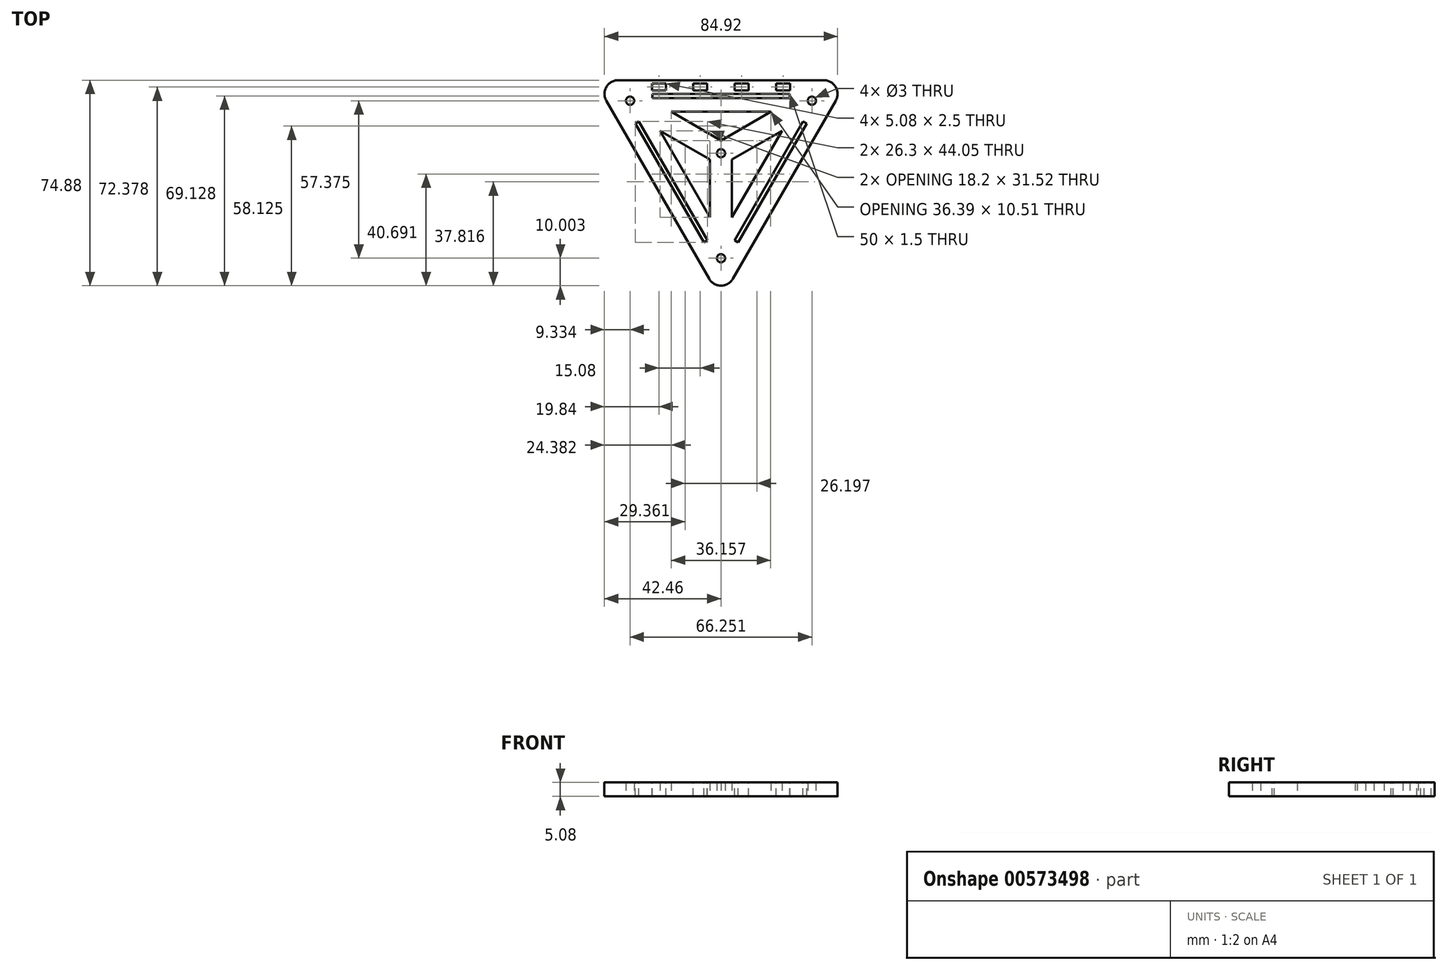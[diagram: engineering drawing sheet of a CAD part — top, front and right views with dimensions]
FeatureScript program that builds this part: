
annotation { "Feature Type Name" : "Feature", "Feature Type Description" : "" }
export const myFeature = defineFeature(function(context is Context, id is Id, definition is map)
    precondition{}
    {
        {
            var Q0;
            Q0=qCreatedBy(makeId("Top.planeOp"),FACE);
            var sketch = newSketch(context, id + "F0", { "sketchPlane" : qUnion([Q0])});
            skLineSegment(sketch, "E0", {"start": v(-33.13, 70.62) * mm, "end": v(33.13, 70.62) * mm, "construction": true});
            skLineSegment(sketch, "E1", {"start": v(33.13, 70.62) * mm, "end": v(0, 13.24) * mm, "construction": true});
            skLineSegment(sketch, "E2", {"start": v(0, 13.24) * mm, "end": v(-33.13, 70.62) * mm, "construction": true});
            skCircle(sketch, "E3", {"center": v(-33.13, 70.62) * mm, "radius": 1.5 * mm});
            skCircle(sketch, "E4", {"center": v(33.13, 70.62) * mm, "radius": 1.5 * mm});
            skCircle(sketch, "E5", {"center": v(0, 13.24) * mm, "radius": 1.5 * mm});
            skCircle(sketch, "E6", {"center": v(0, 51.5) * mm, "radius": 1.5 * mm});
            skPoint(sketch, "E6.centerSnap0", {"position": v(0, 70.62) * mm});
            skLineSegment(sketch, "E7", {"start": v(0, 51.5) * mm, "end": v(-33.13, 70.62) * mm, "construction": true});
            skLineSegment(sketch, "E8", {"start": v(0, 51.5) * mm, "end": v(33.13, 70.62) * mm, "construction": true});
            skLineSegment(sketch, "E9", {"start": v(0, 51.5) * mm, "end": v(0, 13.24) * mm, "construction": true});
            skLineSegment(sketch, "E10", {"start": v(0, -1.76) * mm, "end": v(46.12, 78.12) * mm});
            skLineSegment(sketch, "E11", {"start": v(33.13, 70.62) * mm, "end": v(46.12, 78.12) * mm});
            skLineSegment(sketch, "E12", {"start": v(46.12, 78.12) * mm, "end": v(0, 78.12) * mm});
            skLineSegment(sketch, "E13.MirrorCS", {"start": v(-46.12, 78.12) * mm, "end": v(0, 78.12) * mm});
            skLineSegment(sketch, "E14.MirrorCS", {"start": v(-33.13, 70.62) * mm, "end": v(-46.12, 78.12) * mm});
            skLineSegment(sketch, "E15.MirrorCS", {"start": v(0, -1.76) * mm, "end": v(-46.12, 78.12) * mm});
            skLineSegment(sketch, "E16", {"start": v(0, 66.62) * mm, "end": v(26.2, 66.62) * mm});
            skLineSegment(sketch, "E17", {"start": v(26.2, 66.62) * mm, "end": v(0, 21.24) * mm});
            skLineSegment(sketch, "E18.MirrorCS", {"start": v(0, 66.62) * mm, "end": v(-26.2, 66.62) * mm});
            skLineSegment(sketch, "E19.MirrorCS", {"start": v(-26.2, 66.62) * mm, "end": v(0, 21.24) * mm});
            skLineSegment(sketch, "E20", {"start": v(-22.2, 59.7) * mm, "end": v(-4, 49.18) * mm});
            skLineSegment(sketch, "E21", {"start": v(-4, 49.18) * mm, "end": v(-4, 28.17) * mm});
            skLineSegment(sketch, "E22", {"start": v(-18.2, 66.62) * mm, "end": v(0, 56.11) * mm});
            skLineSegment(sketch, "E23.MirrorCS", {"start": v(18.2, 66.62) * mm, "end": v(0, 56.11) * mm});
            skLineSegment(sketch, "E24.MirrorCS", {"start": v(22.2, 59.7) * mm, "end": v(4, 49.18) * mm});
            skLineSegment(sketch, "E25.MirrorCS", {"start": v(4, 49.18) * mm, "end": v(4, 28.17) * mm});
            skSolve(sketch);
        }
        {
            var Q0;
            Q0=makeQuery(id+"F0.imprint","IMPRINT",FACE,{"disambiguationData":[TD([[makeQuery(id+"F0.imprint","IMPRINT",EDGE,{"derivedFrom":sQuery(id+"F0.wireOp",EDGE,"E3")}),-1.0]])]});
            var Q1;
            Q1=makeQuery(id+"F0.imprint","IMPRINT",FACE,{"disambiguationData":[TD([[makeQuery(id+"F0.imprint","IMPRINT",EDGE,{"derivedFrom":sQuery(id+"F0.wireOp",EDGE,"E6")}),-1.0]])]});
            extrude(context, id + "F1", {"entities" : qUnion([Q0, Q1]), "depth" : 5.08 * mm, "offsetDistance" : 25 * mm});
        }
        {
            var Q0;
            Q0=makeQuery(id+"F1.opExtrude","SWEPT_EDGE",EDGE,{"disambiguationData":[OSD([sQuery(id+"F0.wireOp",EDGE,"E13.MirrorCS"),sQuery(id+"F0.wireOp",EDGE,"E15.MirrorCS")])]});
            var Q1;
            Q1=makeQuery(id+"F1.opExtrude","SWEPT_EDGE",EDGE,{"disambiguationData":[OSD([sQuery(id+"F0.wireOp",EDGE,"E10"),sQuery(id+"F0.wireOp",EDGE,"E15.MirrorCS")])]});
            var Q2;
            Q2=makeQuery(id+"F1.opExtrude","SWEPT_EDGE",EDGE,{"disambiguationData":[OSD([sQuery(id+"F0.wireOp",EDGE,"E10"),sQuery(id+"F0.wireOp",EDGE,"E12")])]});
            fillet(context, id + "F2", {"entities" : qUnion([Q0, Q1, Q2]), "radius" : 5 * mm, "tangentPropagation" : true, "allowEdgeOverflow" : false});
        }
        {
            var Q0;
            Q0=makeQuery(id+"F1.opExtrude","CAP_FACE",FACE,{"disambiguationData":[OSD([sQuery(id+"F0.wireOp",EDGE,"E3"),sQuery(id+"F0.wireOp",EDGE,"E4"),sQuery(id+"F0.wireOp",EDGE,"E5"),sQuery(id+"F0.wireOp",EDGE,"E6"),sQuery(id+"F0.wireOp",EDGE,"E10"),sQuery(id+"F0.wireOp",EDGE,"E12"),sQuery(id+"F0.wireOp",EDGE,"E13.MirrorCS"),sQuery(id+"F0.wireOp",EDGE,"E15.MirrorCS"),sQuery(id+"F0.wireOp",EDGE,"E16"),sQuery(id+"F0.wireOp",EDGE,"E17"),sQuery(id+"F0.wireOp",EDGE,"E18.MirrorCS"),sQuery(id+"F0.wireOp",EDGE,"E19.MirrorCS"),sQuery(id+"F0.wireOp",EDGE,"E20"),sQuery(id+"F0.wireOp",EDGE,"E21"),sQuery(id+"F0.wireOp",EDGE,"E22"),sQuery(id+"F0.wireOp",EDGE,"E23.MirrorCS"),sQuery(id+"F0.wireOp",EDGE,"E24.MirrorCS"),sQuery(id+"F0.wireOp",EDGE,"E25.MirrorCS")])],"isStart":false});
            var sketch = newSketch(context, id + "F3", { "sketchPlane" : qUnion([Q0])});
            skLineSegment(sketch, "E26", {"start": v(0, 78.12) * mm, "end": v(0, 66.62) * mm, "construction": true});
            skLineSegment(sketch, "E27.bottom", {"start": v(25, 73.12) * mm, "end": v(-25, 73.12) * mm});
            skLineSegment(sketch, "E27.top", {"start": v(25, 71.62) * mm, "end": v(-25, 71.62) * mm});
            skLineSegment(sketch, "E27.left", {"start": v(25, 73.12) * mm, "end": v(25, 71.62) * mm});
            skLineSegment(sketch, "E27.right", {"start": v(-25, 73.12) * mm, "end": v(-25, 71.62) * mm});
            skPoint(sketch, "E27.middle", {"position": v(0, 72.37) * mm});
            skLineSegment(sketch, "E28", {"start": v(-13.1, 43.93) * mm, "end": v(-23.06, 38.18) * mm, "construction": true});
            skLineSegment(sketch, "E29", {"start": v(13.1, 43.93) * mm, "end": v(23.06, 38.18) * mm, "construction": true});
            skLineSegment(sketch, "E30", {"start": v(-18.08, 41.06) * mm, "end": v(-5.58, 19.4) * mm, "construction": true});
            skLineSegment(sketch, "E31", {"start": v(-5.58, 19.4) * mm, "end": v(-4.93, 19.78) * mm});
            skLineSegment(sketch, "E32", {"start": v(-4.93, 19.78) * mm, "end": v(-17.43, 41.43) * mm});
            skLineSegment(sketch, "E33.MirrorCS", {"start": v(-6.23, 19.03) * mm, "end": v(-18.73, 40.68) * mm});
            skLineSegment(sketch, "E34.MirrorCS", {"start": v(-5.58, 19.4) * mm, "end": v(-6.23, 19.03) * mm});
            skLineSegment(sketch, "E35.MirrorCS", {"start": v(-29.93, 63.08) * mm, "end": v(-17.43, 41.43) * mm});
            skLineSegment(sketch, "E36.MirrorCS", {"start": v(-31.23, 62.33) * mm, "end": v(-18.73, 40.68) * mm});
            skLineSegment(sketch, "E37.MirrorCS", {"start": v(-18.08, 41.06) * mm, "end": v(-30.58, 62.7) * mm, "construction": true});
            skLineSegment(sketch, "E38.MirrorCS", {"start": v(-30.58, 62.7) * mm, "end": v(-29.93, 63.08) * mm});
            skLineSegment(sketch, "E39.MirrorCS", {"start": v(-30.58, 62.7) * mm, "end": v(-31.23, 62.33) * mm});
            skLineSegment(sketch, "E40.MirrorCS", {"start": v(29.93, 63.08) * mm, "end": v(17.43, 41.43) * mm});
            skLineSegment(sketch, "E41.MirrorCS", {"start": v(31.23, 62.33) * mm, "end": v(18.73, 40.68) * mm});
            skLineSegment(sketch, "E42.MirrorCS", {"start": v(30.58, 62.7) * mm, "end": v(29.93, 63.08) * mm});
            skLineSegment(sketch, "E43.MirrorCS", {"start": v(30.58, 62.7) * mm, "end": v(31.23, 62.33) * mm});
            skLineSegment(sketch, "E44.MirrorCS", {"start": v(18.08, 41.06) * mm, "end": v(30.58, 62.7) * mm, "construction": true});
            skLineSegment(sketch, "E45.MirrorCS", {"start": v(5.58, 19.4) * mm, "end": v(4.93, 19.78) * mm});
            skLineSegment(sketch, "E46.MirrorCS", {"start": v(5.58, 19.4) * mm, "end": v(6.23, 19.03) * mm});
            skLineSegment(sketch, "E47.MirrorCS", {"start": v(18.08, 41.06) * mm, "end": v(5.58, 19.4) * mm, "construction": true});
            skLineSegment(sketch, "E48.MirrorCS", {"start": v(4.93, 19.78) * mm, "end": v(17.43, 41.43) * mm});
            skLineSegment(sketch, "E49.MirrorCS", {"start": v(6.23, 19.03) * mm, "end": v(18.73, 40.68) * mm});
            skLineSegment(sketch, "E50.bottom", {"start": v(5, 76.87) * mm, "end": v(10.08, 76.87) * mm});
            skLineSegment(sketch, "E50.top", {"start": v(5, 74.37) * mm, "end": v(10.08, 74.37) * mm});
            skLineSegment(sketch, "E50.left", {"start": v(5, 76.87) * mm, "end": v(5, 74.37) * mm});
            skLineSegment(sketch, "E50.right", {"start": v(10.08, 76.87) * mm, "end": v(10.08, 74.37) * mm});
            skPoint(sketch, "E50.middle", {"position": v(7.54, 75.62) * mm});
            skLineSegment(sketch, "E51", {"start": v(5, 75.62) * mm, "end": v(0, 75.62) * mm});
            skLineSegment(sketch, "E52.bottom", {"start": v(20.08, 76.87) * mm, "end": v(25.16, 76.87) * mm});
            skLineSegment(sketch, "E52.top", {"start": v(20.08, 74.37) * mm, "end": v(25.16, 74.37) * mm});
            skLineSegment(sketch, "E52.left", {"start": v(20.08, 76.87) * mm, "end": v(20.08, 74.37) * mm});
            skLineSegment(sketch, "E52.right", {"start": v(25.16, 76.87) * mm, "end": v(25.16, 74.37) * mm});
            skLineSegment(sketch, "E53.MirrorCS", {"start": v(-5, 76.87) * mm, "end": v(-10.08, 76.87) * mm});
            skLineSegment(sketch, "E54.MirrorCS", {"start": v(-5, 76.87) * mm, "end": v(-5, 74.37) * mm});
            skLineSegment(sketch, "E55.MirrorCS", {"start": v(-5, 74.37) * mm, "end": v(-10.08, 74.37) * mm});
            skLineSegment(sketch, "E56.MirrorCS", {"start": v(-10.08, 76.87) * mm, "end": v(-10.08, 74.37) * mm});
            skLineSegment(sketch, "E57.MirrorCS", {"start": v(-20.08, 76.87) * mm, "end": v(-25.16, 76.87) * mm});
            skLineSegment(sketch, "E58.MirrorCS", {"start": v(-25.16, 76.87) * mm, "end": v(-25.16, 74.37) * mm});
            skLineSegment(sketch, "E59.MirrorCS", {"start": v(-20.08, 74.37) * mm, "end": v(-25.16, 74.37) * mm});
            skLineSegment(sketch, "E60.MirrorCS", {"start": v(-20.08, 76.87) * mm, "end": v(-20.08, 74.37) * mm});
            skSolve(sketch);
        }
        {
            var Q0;
            {var subQ5=sQuery(id+"F3.wireOp",EDGE,"E27.right");Q0=makeQuery(id+"F3.imprint","IMPRINT",FACE,{"disambiguationData":[TD([[makeQuery(id+"F3.imprint","IMPRINT",EDGE,{"derivedFrom":subQ5}),1.0]])]});}
            var Q1;
            {var subQ5=sQuery(id+"F3.wireOp",EDGE,"E27.left");Q1=makeQuery(id+"F3.imprint","IMPRINT",FACE,{"disambiguationData":[TD([[makeQuery(id+"F3.imprint","IMPRINT",EDGE,{"derivedFrom":subQ5}),-1.0]])]});}
            var Q2;
            Q2=makeQuery(id+"F3.imprint","IMPRINT",FACE,{"disambiguationData":[TD([[makeQuery(id+"F3.imprint","IMPRINT",EDGE,{"derivedFrom":sQuery(id+"F3.wireOp",EDGE,"E31")}),1.0]])]});
            var Q3;
            Q3=makeQuery(id+"F3.imprint","IMPRINT",FACE,{"disambiguationData":[TD([[makeQuery(id+"F3.imprint","IMPRINT",EDGE,{"derivedFrom":sQuery(id+"F3.wireOp",EDGE,"E40.MirrorCS")}),1.0]])]});
            var Q4;
            {var subQ3=sQuery(id+"F3.wireOp",EDGE,"E50.bottom");Q4=makeQuery(id+"F3.imprint","IMPRINT",FACE,{"disambiguationData":[TD([[makeQuery(id+"F3.imprint","IMPRINT",EDGE,{"derivedFrom":subQ3}),-1.0]])]});}
            var Q5;
            Q5=makeQuery(id+"F3.imprint","IMPRINT",FACE,{"disambiguationData":[TD([[makeQuery(id+"F3.imprint","IMPRINT",EDGE,{"derivedFrom":sQuery(id+"F3.wireOp",EDGE,"E52.bottom")}),-1.0]])]});
            var Q6;
            Q6=makeQuery(id+"F3.imprint","IMPRINT",FACE,{"disambiguationData":[TD([[makeQuery(id+"F3.imprint","IMPRINT",EDGE,{"derivedFrom":sQuery(id+"F3.wireOp",EDGE,"E57.MirrorCS")}),1.0]])]});
            var Q7;
            Q7=makeQuery(id+"F3.imprint","IMPRINT",FACE,{"disambiguationData":[TD([[makeQuery(id+"F3.imprint","IMPRINT",EDGE,{"derivedFrom":sQuery(id+"F3.wireOp",EDGE,"E53.MirrorCS")}),1.0]])]});
            extrude(context, id + "F4", {"entities" : qUnion([Q0, Q1, Q2, Q3, Q4, Q5, Q6, Q7]), "operationType" : NewBodyOperationType.REMOVE, "oppositeDirection" : true, "depth" : 25 * mm, "offsetDistance" : 25 * mm});
        }
    });
